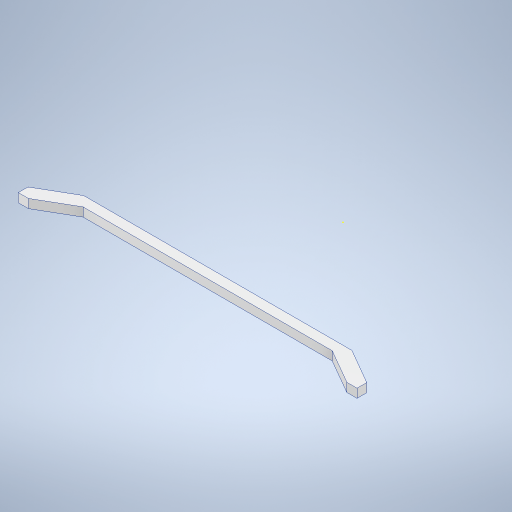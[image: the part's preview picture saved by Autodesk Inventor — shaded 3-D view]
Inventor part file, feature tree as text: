
AUTODESK INVENTOR PART (.ipt)
format: ipt  version: 2024 (Build 280153000, 153)  size: 257,024 bytes
history: native  units: mm
features: sketch x2, extrude x1
ambient origin geometry x8: Origin, YZ Plane, XZ Plane, XY Plane, X Axis, Y Axis, Z Axis, Center Point
bodies: Solid1 (feature_tree)
feature tree (3):
  extrude  "Extrusion1"  Depth=26.0mm TaperAngle=0.0deg
  sketch  "Sketch2"  dims[d5=30.0mm d11=89.0mm d12=30.0mm d13=30.0mm d17=60.0deg d18=60.0deg]
  sketch  "Sketch1"  dims[d0=1000.0mm d1=26.0mm d2=0.0mm]
